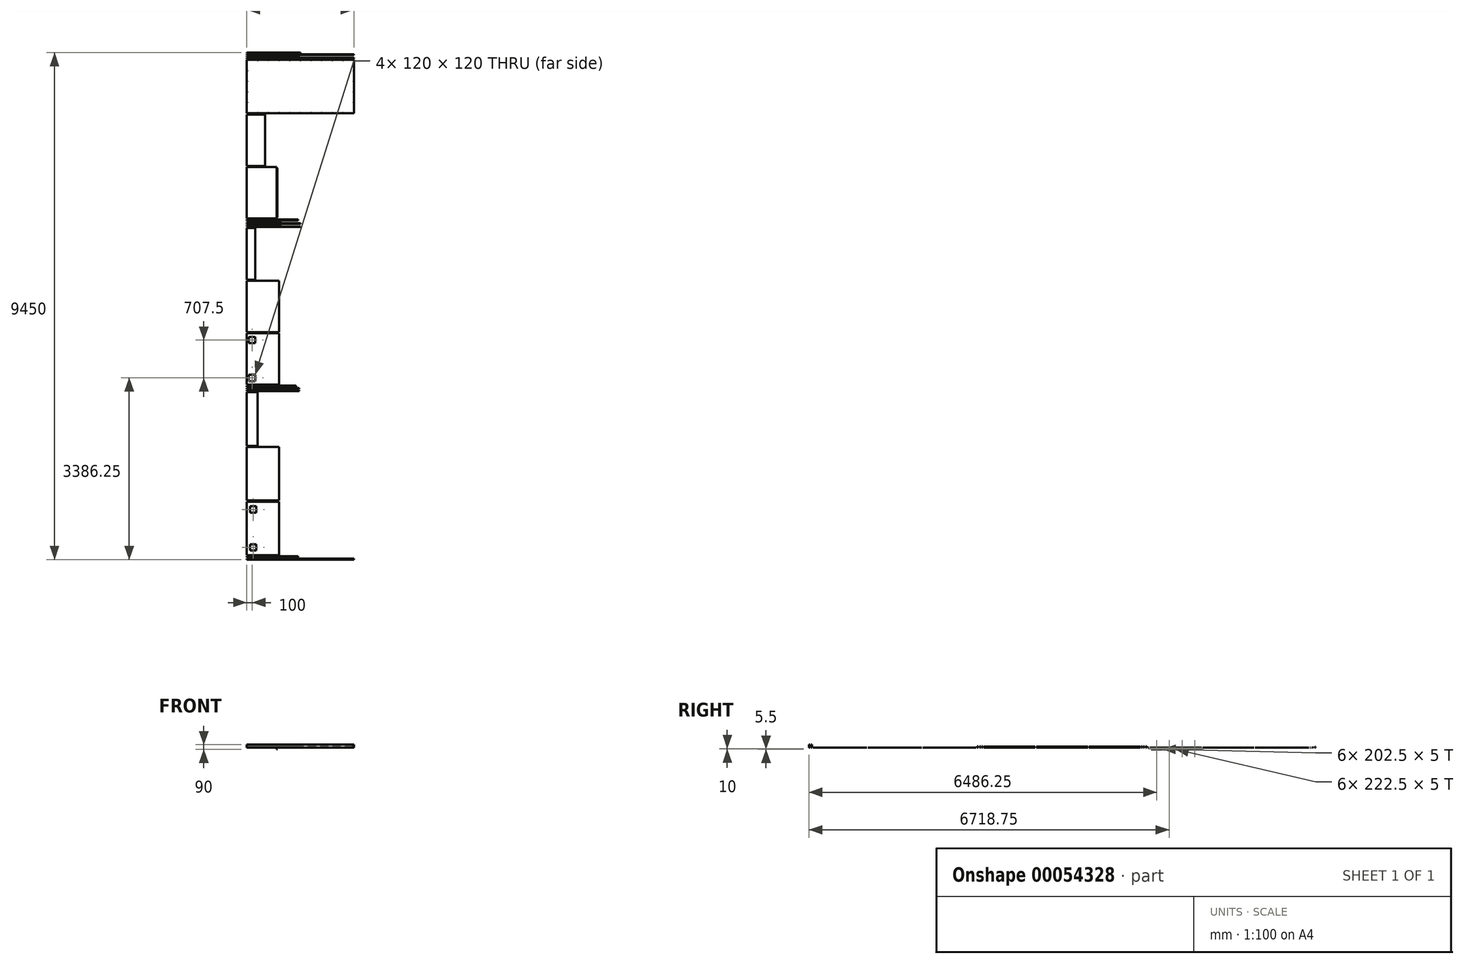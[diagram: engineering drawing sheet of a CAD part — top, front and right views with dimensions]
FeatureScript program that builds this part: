
annotation { "Feature Type Name" : "Feature", "Feature Type Description" : "" }
export const myFeature = defineFeature(function(context is Context, id is Id, definition is map)
    precondition{}
    {
        {
            var Q0;
            Q0=qCreatedBy(makeId("Right.planeOp"),FACE);
            var sketch = newSketch(context, id + "F0", { "sketchPlane" : qUnion([Q0])});
            skLineSegment(sketch, "E0.bottom", {"start": v(0, 60) * mm, "end": v(20, 60) * mm});
            skLineSegment(sketch, "E0.top", {"start": v(0, 0) * mm, "end": v(20, 0) * mm});
            skLineSegment(sketch, "E0.left", {"start": v(0, 60) * mm, "end": v(0, 0) * mm});
            skLineSegment(sketch, "E0.right", {"start": v(20, 60) * mm, "end": v(20, 0) * mm});
            skLineSegment(sketch, "E1.bottom", {"start": v(40, 0) * mm, "end": v(60, 0) * mm});
            skLineSegment(sketch, "E1.top", {"start": v(40, 60) * mm, "end": v(60, 60) * mm});
            skLineSegment(sketch, "E1.left", {"start": v(40, 0) * mm, "end": v(40, 60) * mm});
            skLineSegment(sketch, "E1.right", {"start": v(60, 0) * mm, "end": v(60, 60) * mm});
            skLineSegment(sketch, "E2.bottom", {"start": v(80, 0) * mm, "end": v(1080, 0) * mm});
            skLineSegment(sketch, "E2.top", {"start": v(80, 3) * mm, "end": v(1080, 3) * mm});
            skLineSegment(sketch, "E2.left", {"start": v(80, 0) * mm, "end": v(80, 3) * mm});
            skLineSegment(sketch, "E2.right", {"start": v(1080, 0) * mm, "end": v(1080, 3) * mm});
            skLineSegment(sketch, "E3.bottom", {"start": v(1100, 0) * mm, "end": v(2100, 0) * mm});
            skLineSegment(sketch, "E3.top", {"start": v(1100, 3) * mm, "end": v(2100, 3) * mm});
            skLineSegment(sketch, "E3.left", {"start": v(1100, 0) * mm, "end": v(1100, 3) * mm});
            skLineSegment(sketch, "E3.right", {"start": v(2100, 0) * mm, "end": v(2100, 3) * mm});
            skLineSegment(sketch, "E4.bottom", {"start": v(2120, 0) * mm, "end": v(3120, 0) * mm});
            skLineSegment(sketch, "E4.top", {"start": v(2120, 3) * mm, "end": v(3120, 3) * mm});
            skLineSegment(sketch, "E4.left", {"start": v(2120, 0) * mm, "end": v(2120, 3) * mm});
            skLineSegment(sketch, "E4.right", {"start": v(3120, 0) * mm, "end": v(3120, 3) * mm});
            skLineSegment(sketch, "E5.bottom", {"start": v(3140, 0) * mm, "end": v(3160, 0) * mm});
            skLineSegment(sketch, "E5.top", {"start": v(3140, 30) * mm, "end": v(3160, 30) * mm});
            skLineSegment(sketch, "E5.left", {"start": v(3140, 0) * mm, "end": v(3140, 30) * mm});
            skLineSegment(sketch, "E5.right", {"start": v(3160, 0) * mm, "end": v(3160, 30) * mm});
            skLineSegment(sketch, "E6.bottom", {"start": v(3220, 0) * mm, "end": v(3240, 0) * mm});
            skLineSegment(sketch, "E6.top", {"start": v(3220, 30) * mm, "end": v(3240, 30) * mm});
            skLineSegment(sketch, "E6.left", {"start": v(3220, 0) * mm, "end": v(3220, 30) * mm});
            skLineSegment(sketch, "E6.right", {"start": v(3240, 0) * mm, "end": v(3240, 30) * mm});
            skLineSegment(sketch, "E7.bottom", {"start": v(3260, 0) * mm, "end": v(4220, 0) * mm});
            skLineSegment(sketch, "E7.top", {"start": v(3260, 20) * mm, "end": v(4220, 20) * mm});
            skLineSegment(sketch, "E7.left", {"start": v(3260, 0) * mm, "end": v(3260, 20) * mm});
            skLineSegment(sketch, "E7.right", {"start": v(4220, 0) * mm, "end": v(4220, 20) * mm});
            skLineSegment(sketch, "E8.bottom", {"start": v(4240, 0) * mm, "end": v(5200, 0) * mm});
            skLineSegment(sketch, "E8.top", {"start": v(4240, 20) * mm, "end": v(5200, 20) * mm});
            skLineSegment(sketch, "E8.left", {"start": v(4240, 0) * mm, "end": v(4240, 20) * mm});
            skLineSegment(sketch, "E8.right", {"start": v(5200, 0) * mm, "end": v(5200, 20) * mm});
            skLineSegment(sketch, "E9.bottom", {"start": v(5220, 0) * mm, "end": v(6180, 0) * mm});
            skLineSegment(sketch, "E9.top", {"start": v(5220, 20) * mm, "end": v(6180, 20) * mm});
            skLineSegment(sketch, "E9.left", {"start": v(5220, 0) * mm, "end": v(5220, 20) * mm});
            skLineSegment(sketch, "E9.right", {"start": v(6180, 0) * mm, "end": v(6180, 20) * mm});
            skLineSegment(sketch, "E10.bottom", {"start": v(6200, 0) * mm, "end": v(6210, 0) * mm});
            skLineSegment(sketch, "E10.top", {"start": v(6200, 30) * mm, "end": v(6210, 30) * mm});
            skLineSegment(sketch, "E10.left", {"start": v(6200, 0) * mm, "end": v(6200, 30) * mm});
            skLineSegment(sketch, "E10.right", {"start": v(6210, 0) * mm, "end": v(6210, 30) * mm});
            skLineSegment(sketch, "E11.bottom", {"start": v(6230, 0) * mm, "end": v(6240, 0) * mm});
            skLineSegment(sketch, "E11.top", {"start": v(6230, 30) * mm, "end": v(6240, 30) * mm});
            skLineSegment(sketch, "E11.left", {"start": v(6230, 0) * mm, "end": v(6230, 30) * mm});
            skLineSegment(sketch, "E11.right", {"start": v(6240, 0) * mm, "end": v(6240, 30) * mm});
            skLineSegment(sketch, "E12.bottom", {"start": v(3180, 0) * mm, "end": v(3200, 0) * mm});
            skLineSegment(sketch, "E12.top", {"start": v(3180, 30) * mm, "end": v(3200, 30) * mm});
            skLineSegment(sketch, "E12.left", {"start": v(3180, 0) * mm, "end": v(3180, 30) * mm});
            skLineSegment(sketch, "E12.right", {"start": v(3200, 0) * mm, "end": v(3200, 30) * mm});
            skLineSegment(sketch, "E13.bottom", {"start": v(6260, 0) * mm, "end": v(6270, 0) * mm});
            skLineSegment(sketch, "E13.top", {"start": v(6260, 30) * mm, "end": v(6270, 30) * mm});
            skLineSegment(sketch, "E13.left", {"start": v(6260, 0) * mm, "end": v(6260, 30) * mm});
            skLineSegment(sketch, "E13.right", {"start": v(6270, 0) * mm, "end": v(6270, 30) * mm});
            skLineSegment(sketch, "E14.bottom", {"start": v(6290, 0) * mm, "end": v(6300, 0) * mm});
            skLineSegment(sketch, "E14.top", {"start": v(6290, 30) * mm, "end": v(6300, 30) * mm});
            skLineSegment(sketch, "E14.left", {"start": v(6290, 0) * mm, "end": v(6290, 30) * mm});
            skLineSegment(sketch, "E14.right", {"start": v(6300, 0) * mm, "end": v(6300, 30) * mm});
            skLineSegment(sketch, "E15.bottom", {"start": v(6320, 0) * mm, "end": v(6340, 0) * mm});
            skLineSegment(sketch, "E15.top", {"start": v(6320, 3) * mm, "end": v(6340, 3) * mm});
            skLineSegment(sketch, "E15.left", {"start": v(6320, 0) * mm, "end": v(6320, 3) * mm});
            skLineSegment(sketch, "E15.right", {"start": v(6340, 0) * mm, "end": v(6340, 3) * mm});
            skLineSegment(sketch, "E16.bottom", {"start": v(6360, 0) * mm, "end": v(7320, 0) * mm});
            skLineSegment(sketch, "E16.top", {"start": v(6360, 1) * mm, "end": v(7320, 1) * mm});
            skLineSegment(sketch, "E16.left", {"start": v(6360, 0) * mm, "end": v(6360, 1) * mm});
            skLineSegment(sketch, "E16.right", {"start": v(7320, 0) * mm, "end": v(7320, 1) * mm});
            skLineSegment(sketch, "E17.bottom", {"start": v(7340, 0) * mm, "end": v(8300, 0) * mm});
            skLineSegment(sketch, "E17.top", {"start": v(7340, 1) * mm, "end": v(8300, 1) * mm});
            skLineSegment(sketch, "E17.left", {"start": v(7340, 0) * mm, "end": v(7340, 1) * mm});
            skLineSegment(sketch, "E17.right", {"start": v(8300, 0) * mm, "end": v(8300, 1) * mm});
            skLineSegment(sketch, "E18.bottom", {"start": v(8320, 0) * mm, "end": v(9320, 0) * mm});
            skLineSegment(sketch, "E18.top", {"start": v(8320, 5) * mm, "end": v(9320, 5) * mm});
            skLineSegment(sketch, "E18.left", {"start": v(8320, 0) * mm, "end": v(8320, 5) * mm});
            skLineSegment(sketch, "E18.right", {"start": v(9320, 0) * mm, "end": v(9320, 5) * mm});
            skLineSegment(sketch, "E19.bottom", {"start": v(9340, 0) * mm, "end": v(9355, 0) * mm});
            skLineSegment(sketch, "E19.top", {"start": v(9340, 3) * mm, "end": v(9355, 3) * mm});
            skLineSegment(sketch, "E19.left", {"start": v(9340, 0) * mm, "end": v(9340, 3) * mm});
            skLineSegment(sketch, "E19.right", {"start": v(9355, 0) * mm, "end": v(9355, 3) * mm});
            skLineSegment(sketch, "E20.bottom", {"start": v(9375, 0) * mm, "end": v(9390, 0) * mm});
            skLineSegment(sketch, "E20.top", {"start": v(9375, 3) * mm, "end": v(9390, 3) * mm});
            skLineSegment(sketch, "E20.left", {"start": v(9375, 0) * mm, "end": v(9375, 3) * mm});
            skLineSegment(sketch, "E20.right", {"start": v(9390, 0) * mm, "end": v(9390, 3) * mm});
            skLineSegment(sketch, "E21", {"start": v(9410, 0) * mm, "end": v(9410, 20) * mm});
            skLineSegment(sketch, "E22", {"start": v(9410, 20) * mm, "end": v(9412, 20) * mm});
            skLineSegment(sketch, "E23", {"start": v(9412, 20) * mm, "end": v(9412, 2) * mm});
            skLineSegment(sketch, "E24", {"start": v(9412, 2) * mm, "end": v(9420, 2) * mm});
            skLineSegment(sketch, "E25", {"start": v(9420, 2) * mm, "end": v(9420, 0) * mm});
            skLineSegment(sketch, "E26", {"start": v(9420, 0) * mm, "end": v(9410, 0) * mm});
            skLineSegment(sketch, "E27", {"start": v(9440, 0) * mm, "end": v(9440, 20) * mm});
            skLineSegment(sketch, "E28", {"start": v(9440, 20) * mm, "end": v(9442, 20) * mm});
            skLineSegment(sketch, "E29", {"start": v(9442, 20) * mm, "end": v(9442, 2) * mm});
            skLineSegment(sketch, "E30", {"start": v(9442, 2) * mm, "end": v(9450, 2) * mm});
            skLineSegment(sketch, "E31", {"start": v(9450, 2) * mm, "end": v(9450, 0) * mm});
            skLineSegment(sketch, "E32", {"start": v(9450, 0) * mm, "end": v(9440, 0) * mm});
            skSolve(sketch);
        }
        {
            var Q0;
            Q0=makeQuery(id+"F0.imprint","IMPRINT",FACE,{"disambiguationData":[TD([[makeQuery(id+"F0.imprint","IMPRINT",EDGE,{"derivedFrom":sQuery(id+"F0.wireOp",EDGE,"E0.bottom")}),-1.0]])]});
            extrude(context, id + "F1", {"entities" : qUnion([Q0]), "depth" : 2000 * mm});
        }
        {
            var Q0;
            Q0=makeQuery(id+"F1.opExtrude","SWEPT_FACE",FACE,{"disambiguationData":[OSD([sQuery(id+"F0.wireOp",EDGE,"E0.left")])]});
            var sketch = newSketch(context, id + "F2", { "sketchPlane" : qUnion([Q0])});
            skPoint(sketch, "E33", {"position": v(10, 20) * mm});
            skPoint(sketch, "E34.0.1.0", {"position": v(10, 40) * mm});
            skLineSegment(sketch, "E34.direction1", {"start": v(10, 20) * mm, "end": v(1980, 20) * mm, "construction": true});
            skLineSegment(sketch, "E34.direction2", {"start": v(10, 20) * mm, "end": v(10, 40) * mm, "construction": true});
            skPoint(sketch, "E35.0.1.0", {"position": v(1980, 20) * mm});
            skPoint(sketch, "E35.0.1.1", {"position": v(1980, 40) * mm});
            skSolve(sketch);
        }
        {
            var Q0;
            Q0=sQuery(id+"F2.wireOp",VERTEX,"E33");
            var Q1;
            Q1=sQuery(id+"F2.wireOp",VERTEX,"E34.0.1.0");
            var Q2;
            Q2=sQuery(id+"F2.wireOp",VERTEX,"E35.0.1.1");
            var Q3;
            Q3=sQuery(id+"F2.wireOp",VERTEX,"E35.0.1.0");
            var Q4;
            Q4=makeQuery(id+"F1.opExtrude","SWEPT_BODY",BODY,{"disambiguationData":[OSD([sQuery(id+"F0.wireOp",EDGE,"E0.bottom"),sQuery(id+"F0.wireOp",EDGE,"E0.top"),sQuery(id+"F0.wireOp",EDGE,"E0.left"),sQuery(id+"F0.wireOp",EDGE,"E0.right")])]});
            hole(context, id + "F3", {"style" : HoleStyle.SIMPLE, "endStyle" : HoleEndStyle.THROUGH, "holeDiameter" : 2 * mm, "tappedDepth" : 10.5 * mm, "tapClearance" : 3, "locations" : qUnion([Q0, Q1, Q2, Q3]), "scope" : qUnion([Q4])});
        }
        {
            var Q0;
            Q0=makeQuery(id+"F0.imprint","IMPRINT",FACE,{"disambiguationData":[TD([[makeQuery(id+"F0.imprint","IMPRINT",EDGE,{"derivedFrom":sQuery(id+"F0.wireOp",EDGE,"E1.bottom")}),1.0]])]});
            extrude(context, id + "F4", {"entities" : qUnion([Q0]), "depth" : (1000 - 40) * mm});
        }
        {
            var Q0;
            Q0=makeQuery(id+"F0.imprint","IMPRINT",FACE,{"disambiguationData":[TD([[makeQuery(id+"F0.imprint","IMPRINT",EDGE,{"derivedFrom":sQuery(id+"F0.wireOp",EDGE,"E1.bottom")}),1.0]])]});
            var sketch = newSketch(context, id + "F5", { "sketchPlane" : qUnion([Q0])});
            skPoint(sketch, "E36", {"position": v(50, 40) * mm});
            skPoint(sketch, "E37", {"position": v(50, 20) * mm});
            skSolve(sketch);
        }
        {
            var Q0;
            Q0=makeQuery(id+"F4.opExtrude","CAP_FACE",FACE,{"disambiguationData":[OSD([sQuery(id+"F0.wireOp",EDGE,"E1.bottom"),sQuery(id+"F0.wireOp",EDGE,"E1.top"),sQuery(id+"F0.wireOp",EDGE,"E1.left"),sQuery(id+"F0.wireOp",EDGE,"E1.right")])],"isStart":false});
            var sketch = newSketch(context, id + "F6", { "sketchPlane" : qUnion([Q0])});
            skPoint(sketch, "E38", {"position": v(50, 20) * mm});
            skPoint(sketch, "E39", {"position": v(50, 40) * mm});
            skSolve(sketch);
        }
        {
            var Q0;
            Q0=sQuery(id+"F5.wireOp",VERTEX,"E36");
            var Q1;
            Q1=sQuery(id+"F6.wireOp",VERTEX,"E39");
            var Q2;
            Q2=makeQuery(id+"F4.opExtrude","SWEPT_BODY",BODY,{"disambiguationData":[OSD([sQuery(id+"F0.wireOp",EDGE,"E1.bottom"),sQuery(id+"F0.wireOp",EDGE,"E1.top"),sQuery(id+"F0.wireOp",EDGE,"E1.left"),sQuery(id+"F0.wireOp",EDGE,"E1.right")])]});
            hole(context, id + "F7", {"style" : HoleStyle.SIMPLE, "endStyle" : HoleEndStyle.BLIND, "holeDiameter" : 2 * mm, "holeDepth" : 50 * mm, "tappedDepth" : 10.5 * mm, "tapClearance" : 3, "locations" : qUnion([Q0, Q1]), "scope" : qUnion([Q2])});
        }
        {
            var Q0;
            Q0=sQuery(id+"F5.wireOp",VERTEX,"E36");
            var Q1;
            Q1=sQuery(id+"F5.wireOp",VERTEX,"E37");
            var Q2;
            Q2=makeQuery(id+"F4.opExtrude","SWEPT_BODY",BODY,{"disambiguationData":[OSD([sQuery(id+"F0.wireOp",EDGE,"E1.bottom"),sQuery(id+"F0.wireOp",EDGE,"E1.top"),sQuery(id+"F0.wireOp",EDGE,"E1.left"),sQuery(id+"F0.wireOp",EDGE,"E1.right")])]});
            hole(context, id + "F8", {"style" : HoleStyle.SIMPLE, "endStyle" : HoleEndStyle.BLIND, "oppositeDirection" : true, "holeDiameter" : 2 * mm, "holeDepth" : 50 * mm, "tappedDepth" : 10.5 * mm, "tapClearance" : 3, "locations" : qUnion([Q0, Q1]), "scope" : qUnion([Q2])});
        }
        {
            var Q0;
            Q0=makeQuery(id+"F0.imprint","IMPRINT",FACE,{"disambiguationData":[TD([[makeQuery(id+"F0.imprint","IMPRINT",EDGE,{"derivedFrom":sQuery(id+"F0.wireOp",EDGE,"E2.bottom")}),1.0]])]});
            extrude(context, id + "F9", {"entities" : qUnion([Q0]), "depth" : 600 * mm});
        }
        {
            var Q0;
            Q0=makeQuery(id+"F9.opExtrude","SWEPT_FACE",FACE,{"disambiguationData":[OSD([sQuery(id+"F0.wireOp",EDGE,"E2.top")])]});
            var sketch = newSketch(context, id + "F10", { "sketchPlane" : qUnion([Q0])});
            skLineSegment(sketch, "E40.bottom", {"start": v(60, 166.25) * mm, "end": v(180, 166.25) * mm});
            skLineSegment(sketch, "E40.top", {"start": v(60, 286.25) * mm, "end": v(180, 286.25) * mm});
            skLineSegment(sketch, "E40.left", {"start": v(60, 166.25) * mm, "end": v(60, 286.25) * mm});
            skLineSegment(sketch, "E40.right", {"start": v(180, 166.25) * mm, "end": v(180, 286.25) * mm});
            skLineSegment(sketch, "E41.bottom", {"start": v(60, 873.75) * mm, "end": v(180, 873.75) * mm});
            skLineSegment(sketch, "E41.top", {"start": v(60, 993.75) * mm, "end": v(180, 993.75) * mm});
            skLineSegment(sketch, "E41.left", {"start": v(60, 873.75) * mm, "end": v(60, 993.75) * mm});
            skLineSegment(sketch, "E41.right", {"start": v(180, 873.75) * mm, "end": v(180, 993.75) * mm});
            skSolve(sketch);
        }
        {
            var Q0;
            Q0=makeQuery(id+"F10.imprint","IMPRINT",FACE,{"disambiguationData":[TD([[makeQuery(id+"F10.imprint","IMPRINT",EDGE,{"derivedFrom":sQuery(id+"F10.wireOp",EDGE,"E40.bottom")}),1.0]])]});
            var Q1;
            Q1=makeQuery(id+"F10.imprint","IMPRINT",FACE,{"disambiguationData":[TD([[makeQuery(id+"F10.imprint","IMPRINT",EDGE,{"derivedFrom":sQuery(id+"F10.wireOp",EDGE,"E41.bottom")}),1.0]])]});
            extrude(context, id + "F11", {"entities" : qUnion([Q0, Q1]), "operationType" : NewBodyOperationType.REMOVE, "endBound" : BoundingType.UP_TO_NEXT, "oppositeDirection" : true, "depth" : 25 * mm});
        }
        {
            var Q0;
            Q0=makeQuery(id+"F0.imprint","IMPRINT",FACE,{"disambiguationData":[TD([[makeQuery(id+"F0.imprint","IMPRINT",EDGE,{"derivedFrom":sQuery(id+"F0.wireOp",EDGE,"E3.bottom")}),1.0]])]});
            var Q1;
            Q1=makeQuery(id+"F9.opExtrude","CAP_FACE",FACE,{"disambiguationData":[OSD([sQuery(id+"F0.wireOp",EDGE,"E2.bottom"),sQuery(id+"F0.wireOp",EDGE,"E2.top"),sQuery(id+"F0.wireOp",EDGE,"E2.left"),sQuery(id+"F0.wireOp",EDGE,"E2.right")])],"isStart":false});
            extrude(context, id + "F12", {"entities" : qUnion([Q0]), "endBound" : BoundingType.UP_TO_SURFACE, "endBoundEntityFace" : qUnion([Q1]), "depth" : 25 * mm});
        }
        {
            var Q0;
            Q0=makeQuery(id+"F0.imprint","IMPRINT",FACE,{"disambiguationData":[TD([[makeQuery(id+"F0.imprint","IMPRINT",EDGE,{"derivedFrom":sQuery(id+"F0.wireOp",EDGE,"E4.bottom")}),1.0]])]});
            extrude(context, id + "F13", {"entities" : qUnion([Q0]), "depth" : 200 * mm});
        }
        {
            var Q0;
            Q0=makeQuery(id+"F0.imprint","IMPRINT",FACE,{"disambiguationData":[TD([[makeQuery(id+"F0.imprint","IMPRINT",EDGE,{"derivedFrom":sQuery(id+"F0.wireOp",EDGE,"E5.bottom")}),1.0]])]});
            extrude(context, id + "F14", {"entities" : qUnion([Q0]), "depth" : (1000 - 20) * mm});
        }
        {
            var Q0;
            Q0=makeQuery(id+"F0.imprint","IMPRINT",FACE,{"disambiguationData":[TD([[makeQuery(id+"F0.imprint","IMPRINT",EDGE,{"derivedFrom":sQuery(id+"F0.wireOp",EDGE,"E6.bottom")}),1.0]])]});
            extrude(context, id + "F15", {"entities" : qUnion([Q0]), "depth" : (960 - 40) * mm});
        }
        {
            var Q0;
            Q0=makeQuery(id+"F0.imprint","IMPRINT",FACE,{"disambiguationData":[TD([[makeQuery(id+"F0.imprint","IMPRINT",EDGE,{"derivedFrom":sQuery(id+"F0.wireOp",EDGE,"E7.bottom")}),1.0]])]});
            extrude(context, id + "F16", {"entities" : qUnion([Q0]), "depth" : 600 * mm});
        }
        {
            var Q0;
            Q0=makeQuery(id+"F16.opExtrude","SWEPT_FACE",FACE,{"disambiguationData":[OSD([sQuery(id+"F0.wireOp",EDGE,"E7.top")])]});
            var sketch = newSketch(context, id + "F17", { "sketchPlane" : qUnion([Q0])});
            skLineSegment(sketch, "E42.bottom", {"start": v(40, 3326.25) * mm, "end": v(160, 3326.25) * mm});
            skLineSegment(sketch, "E42.top", {"start": v(40, 3446.25) * mm, "end": v(160, 3446.25) * mm});
            skLineSegment(sketch, "E42.left", {"start": v(40, 3326.25) * mm, "end": v(40, 3446.25) * mm});
            skLineSegment(sketch, "E42.right", {"start": v(160, 3326.25) * mm, "end": v(160, 3446.25) * mm});
            skLineSegment(sketch, "E43.bottom", {"start": v(160, 4033.75) * mm, "end": v(40, 4033.75) * mm});
            skLineSegment(sketch, "E43.top", {"start": v(160, 4153.75) * mm, "end": v(40, 4153.75) * mm});
            skLineSegment(sketch, "E43.left", {"start": v(160, 4033.75) * mm, "end": v(160, 4153.75) * mm});
            skLineSegment(sketch, "E43.right", {"start": v(40, 4033.75) * mm, "end": v(40, 4153.75) * mm});
            skSolve(sketch);
        }
        {
            var Q0;
            Q0=makeQuery(id+"F17.imprint","IMPRINT",FACE,{"disambiguationData":[TD([[makeQuery(id+"F17.imprint","IMPRINT",EDGE,{"derivedFrom":sQuery(id+"F17.wireOp",EDGE,"E42.bottom")}),1.0]])]});
            var Q1;
            Q1=makeQuery(id+"F17.imprint","IMPRINT",FACE,{"disambiguationData":[TD([[makeQuery(id+"F17.imprint","IMPRINT",EDGE,{"derivedFrom":sQuery(id+"F17.wireOp",EDGE,"E43.bottom")}),-1.0]])]});
            extrude(context, id + "F18", {"entities" : qUnion([Q0, Q1]), "operationType" : NewBodyOperationType.REMOVE, "endBound" : BoundingType.UP_TO_NEXT, "oppositeDirection" : true, "depth" : 25 * mm});
        }
        {
            var Q0;
            Q0=makeQuery(id+"F0.imprint","IMPRINT",FACE,{"disambiguationData":[TD([[makeQuery(id+"F0.imprint","IMPRINT",EDGE,{"derivedFrom":sQuery(id+"F0.wireOp",EDGE,"E8.bottom")}),1.0]])]});
            extrude(context, id + "F19", {"entities" : qUnion([Q0]), "depth" : 600 * mm});
        }
        {
            var Q0;
            Q0=makeQuery(id+"F0.imprint","IMPRINT",FACE,{"disambiguationData":[TD([[makeQuery(id+"F0.imprint","IMPRINT",EDGE,{"derivedFrom":sQuery(id+"F0.wireOp",EDGE,"E9.bottom")}),1.0]])]});
            extrude(context, id + "F20", {"entities" : qUnion([Q0]), "depth" : (200 - 40) * mm});
        }
        {
            var Q0;
            Q0=makeQuery(id+"F0.imprint","IMPRINT",FACE,{"disambiguationData":[TD([[makeQuery(id+"F0.imprint","IMPRINT",EDGE,{"derivedFrom":sQuery(id+"F0.wireOp",EDGE,"E10.bottom")}),1.0]])]});
            extrude(context, id + "F21", {"entities" : qUnion([Q0]), "depth" : 1000 * mm});
        }
        {
            var Q0;
            Q0=makeQuery(id+"F0.imprint","IMPRINT",FACE,{"disambiguationData":[TD([[makeQuery(id+"F0.imprint","IMPRINT",EDGE,{"derivedFrom":sQuery(id+"F0.wireOp",EDGE,"E11.bottom")}),1.0]])]});
            extrude(context, id + "F22", {"entities" : qUnion([Q0]), "depth" : 625 * mm});
        }
        {
            var Q0;
            Q0=makeQuery(id+"F14.opExtrude","SWEPT_FACE",FACE,{"disambiguationData":[OSD([sQuery(id+"F0.wireOp",EDGE,"E5.top")])]});
            var sketch = newSketch(context, id + "F23", { "sketchPlane" : qUnion([Q0])});
            skLineSegment(sketch, "E44.bottom", {"start": v(539, 3140) * mm, "end": v(559, 3140) * mm});
            skLineSegment(sketch, "E44.top", {"start": v(539, 3160) * mm, "end": v(559, 3160) * mm});
            skLineSegment(sketch, "E44.left", {"start": v(539, 3140) * mm, "end": v(539, 3160) * mm});
            skLineSegment(sketch, "E44.right", {"start": v(559, 3140) * mm, "end": v(559, 3160) * mm});
            skSolve(sketch);
        }
        {
            var Q0;
            Q0=makeQuery(id+"F23.imprint","IMPRINT",FACE,{"disambiguationData":[TD([[makeQuery(id+"F23.imprint","IMPRINT",EDGE,{"derivedFrom":sQuery(id+"F23.wireOp",EDGE,"E44.bottom")}),-1.0]])]});
            extrude(context, id + "F24", {"entities" : qUnion([Q0]), "operationType" : NewBodyOperationType.REMOVE, "oppositeDirection" : true, "depth" : 3 * mm});
        }
        {
            var Q0;
            Q0=makeQuery(id+"F0.imprint","IMPRINT",FACE,{"disambiguationData":[TD([[makeQuery(id+"F0.imprint","IMPRINT",EDGE,{"derivedFrom":sQuery(id+"F0.wireOp",EDGE,"E12.bottom")}),1.0]])]});
            extrude(context, id + "F25", {"entities" : qUnion([Q0]), "depth" : 980 * mm});
        }
        {
            var Q0;
            Q0=makeQuery(id+"F25.opExtrude","SWEPT_FACE",FACE,{"disambiguationData":[OSD([sQuery(id+"F0.wireOp",EDGE,"E12.top")])]});
            var sketch = newSketch(context, id + "F26", { "sketchPlane" : qUnion([Q0])});
            skLineSegment(sketch, "E45.bottom", {"start": v(98, 3180) * mm, "end": v(118, 3180) * mm});
            skLineSegment(sketch, "E45.top", {"start": v(98, 3200) * mm, "end": v(118, 3200) * mm});
            skLineSegment(sketch, "E45.left", {"start": v(98, 3180) * mm, "end": v(98, 3200) * mm});
            skLineSegment(sketch, "E45.right", {"start": v(118, 3180) * mm, "end": v(118, 3200) * mm});
            skLineSegment(sketch, "E46.bottom", {"start": v(637, 3180) * mm, "end": v(657, 3180) * mm});
            skLineSegment(sketch, "E46.top", {"start": v(637, 3200) * mm, "end": v(657, 3200) * mm});
            skLineSegment(sketch, "E46.left", {"start": v(637, 3180) * mm, "end": v(637, 3200) * mm});
            skLineSegment(sketch, "E46.right", {"start": v(657, 3180) * mm, "end": v(657, 3200) * mm});
            skSolve(sketch);
        }
        {
            var Q0;
            Q0=makeQuery(id+"F26.imprint","IMPRINT",FACE,{"disambiguationData":[TD([[makeQuery(id+"F26.imprint","IMPRINT",EDGE,{"derivedFrom":sQuery(id+"F26.wireOp",EDGE,"E46.bottom")}),-1.0]])]});
            var Q1;
            Q1=makeQuery(id+"F26.imprint","IMPRINT",FACE,{"disambiguationData":[TD([[makeQuery(id+"F26.imprint","IMPRINT",EDGE,{"derivedFrom":sQuery(id+"F26.wireOp",EDGE,"E45.bottom")}),-1.0]])]});
            extrude(context, id + "F27", {"entities" : qUnion([Q0, Q1]), "operationType" : NewBodyOperationType.REMOVE, "oppositeDirection" : true, "depth" : 3 * mm});
        }
        {
            var Q0;
            Q0=makeQuery(id+"F21.opExtrude","SWEPT_FACE",FACE,{"disambiguationData":[OSD([sQuery(id+"F0.wireOp",EDGE,"E10.top")])]});
            var sketch = newSketch(context, id + "F28", { "sketchPlane" : qUnion([Q0])});
            skLineSegment(sketch, "E47.bottom", {"start": v(519, 6200) * mm, "end": v(539, 6200) * mm});
            skLineSegment(sketch, "E47.top", {"start": v(519, 6210) * mm, "end": v(539, 6210) * mm});
            skLineSegment(sketch, "E47.left", {"start": v(519, 6200) * mm, "end": v(519, 6210) * mm});
            skLineSegment(sketch, "E47.right", {"start": v(539, 6200) * mm, "end": v(539, 6210) * mm});
            skSolve(sketch);
        }
        {
            var Q0;
            Q0=makeQuery(id+"F28.imprint","IMPRINT",FACE,{"disambiguationData":[TD([[makeQuery(id+"F28.imprint","IMPRINT",EDGE,{"derivedFrom":sQuery(id+"F28.wireOp",EDGE,"E47.bottom")}),-1.0]])]});
            extrude(context, id + "F29", {"entities" : qUnion([Q0]), "operationType" : NewBodyOperationType.REMOVE, "oppositeDirection" : true, "depth" : 3 * mm});
        }
        {
            var Q0;
            Q0=makeQuery(id+"F22.opExtrude","SWEPT_FACE",FACE,{"disambiguationData":[OSD([sQuery(id+"F0.wireOp",EDGE,"E11.top")])]});
            var sketch = newSketch(context, id + "F30", { "sketchPlane" : qUnion([Q0])});
            skLineSegment(sketch, "E48.bottom", {"start": v(58, 6230) * mm, "end": v(78, 6230) * mm});
            skLineSegment(sketch, "E48.top", {"start": v(58, 6240) * mm, "end": v(78, 6240) * mm});
            skLineSegment(sketch, "E48.left", {"start": v(58, 6230) * mm, "end": v(58, 6240) * mm});
            skLineSegment(sketch, "E48.right", {"start": v(78, 6230) * mm, "end": v(78, 6240) * mm});
            skLineSegment(sketch, "E49.bottom", {"start": v(597, 6230) * mm, "end": v(617, 6230) * mm});
            skLineSegment(sketch, "E49.top", {"start": v(597, 6240) * mm, "end": v(617, 6240) * mm});
            skLineSegment(sketch, "E49.left", {"start": v(597, 6230) * mm, "end": v(597, 6240) * mm});
            skLineSegment(sketch, "E49.right", {"start": v(617, 6230) * mm, "end": v(617, 6240) * mm});
            skSolve(sketch);
        }
        {
            var Q0;
            Q0=makeQuery(id+"F30.imprint","IMPRINT",FACE,{"disambiguationData":[TD([[makeQuery(id+"F30.imprint","IMPRINT",EDGE,{"derivedFrom":sQuery(id+"F30.wireOp",EDGE,"E48.bottom")}),-1.0]])]});
            var Q1;
            Q1=makeQuery(id+"F30.imprint","IMPRINT",FACE,{"disambiguationData":[TD([[makeQuery(id+"F30.imprint","IMPRINT",EDGE,{"derivedFrom":sQuery(id+"F30.wireOp",EDGE,"E49.bottom")}),-1.0]])]});
            extrude(context, id + "F31", {"entities" : qUnion([Q0, Q1]), "operationType" : NewBodyOperationType.REMOVE, "oppositeDirection" : true, "depth" : 3 * mm});
        }
        {
            var Q0;
            Q0=makeQuery(id+"F0.imprint","IMPRINT",FACE,{"disambiguationData":[TD([[makeQuery(id+"F0.imprint","IMPRINT",EDGE,{"derivedFrom":sQuery(id+"F0.wireOp",EDGE,"E13.bottom")}),1.0]])]});
            var Q1;
            Q1=makeQuery(id+"F21.opExtrude","CAP_FACE",FACE,{"disambiguationData":[OSD([sQuery(id+"F0.wireOp",EDGE,"E10.bottom"),sQuery(id+"F0.wireOp",EDGE,"E10.top"),sQuery(id+"F0.wireOp",EDGE,"E10.left"),sQuery(id+"F0.wireOp",EDGE,"E10.right")])],"isStart":false});
            extrude(context, id + "F32", {"entities" : qUnion([Q0]), "endBound" : BoundingType.UP_TO_SURFACE, "endBoundEntityFace" : qUnion([Q1]), "depth" : 1000 * mm});
        }
        {
            var Q0;
            Q0=makeQuery(id+"F0.imprint","IMPRINT",FACE,{"disambiguationData":[TD([[makeQuery(id+"F0.imprint","IMPRINT",EDGE,{"derivedFrom":sQuery(id+"F0.wireOp",EDGE,"E14.bottom")}),1.0]])]});
            var Q1;
            Q1=makeQuery(id+"F22.opExtrude","CAP_FACE",FACE,{"disambiguationData":[OSD([sQuery(id+"F0.wireOp",EDGE,"E11.bottom"),sQuery(id+"F0.wireOp",EDGE,"E11.top"),sQuery(id+"F0.wireOp",EDGE,"E11.left"),sQuery(id+"F0.wireOp",EDGE,"E11.right")])],"isStart":false});
            extrude(context, id + "F33", {"entities" : qUnion([Q0]), "endBound" : BoundingType.UP_TO_SURFACE, "endBoundEntityFace" : qUnion([Q1]), "depth" : 25 * mm});
        }
        {
            var Q0;
            Q0=makeQuery(id+"F32.opExtrude","SWEPT_FACE",FACE,{"disambiguationData":[OSD([sQuery(id+"F0.wireOp",EDGE,"E13.top")])]});
            var sketch = newSketch(context, id + "F34", { "sketchPlane" : qUnion([Q0])});
            skLineSegment(sketch, "E50.bottom", {"start": v(303, 6260) * mm, "end": v(323, 6260) * mm});
            skLineSegment(sketch, "E50.top", {"start": v(303, 6270) * mm, "end": v(323, 6270) * mm});
            skLineSegment(sketch, "E50.left", {"start": v(303, 6260) * mm, "end": v(303, 6270) * mm});
            skLineSegment(sketch, "E50.right", {"start": v(323, 6260) * mm, "end": v(323, 6270) * mm});
            skLineSegment(sketch, "E51.bottom", {"start": v(842, 6260) * mm, "end": v(862, 6260) * mm});
            skLineSegment(sketch, "E51.top", {"start": v(842, 6270) * mm, "end": v(862, 6270) * mm});
            skLineSegment(sketch, "E51.left", {"start": v(842, 6260) * mm, "end": v(842, 6270) * mm});
            skLineSegment(sketch, "E51.right", {"start": v(862, 6260) * mm, "end": v(862, 6270) * mm});
            skSolve(sketch);
        }
        {
            var Q0;
            Q0=makeQuery(id+"F34.imprint","IMPRINT",FACE,{"disambiguationData":[TD([[makeQuery(id+"F34.imprint","IMPRINT",EDGE,{"derivedFrom":sQuery(id+"F34.wireOp",EDGE,"E50.bottom")}),-1.0]])]});
            var Q1;
            Q1=makeQuery(id+"F34.imprint","IMPRINT",FACE,{"disambiguationData":[TD([[makeQuery(id+"F34.imprint","IMPRINT",EDGE,{"derivedFrom":sQuery(id+"F34.wireOp",EDGE,"E51.bottom")}),-1.0]])]});
            extrude(context, id + "F35", {"entities" : qUnion([Q0, Q1]), "operationType" : NewBodyOperationType.REMOVE, "oppositeDirection" : true, "depth" : 3 * mm});
        }
        {
            var Q0;
            Q0=makeQuery(id+"F33.opExtrude","SWEPT_FACE",FACE,{"disambiguationData":[OSD([sQuery(id+"F0.wireOp",EDGE,"E14.top")])]});
            var sketch = newSketch(context, id + "F36", { "sketchPlane" : qUnion([Q0])});
            skLineSegment(sketch, "E52.bottom", {"start": v(381, 6290) * mm, "end": v(401, 6290) * mm});
            skLineSegment(sketch, "E52.top", {"start": v(381, 6300) * mm, "end": v(401, 6300) * mm});
            skLineSegment(sketch, "E52.left", {"start": v(381, 6290) * mm, "end": v(381, 6300) * mm});
            skLineSegment(sketch, "E52.right", {"start": v(401, 6290) * mm, "end": v(401, 6300) * mm});
            skSolve(sketch);
        }
        {
            var Q0;
            Q0=makeQuery(id+"F36.imprint","IMPRINT",FACE,{"disambiguationData":[TD([[makeQuery(id+"F36.imprint","IMPRINT",EDGE,{"derivedFrom":sQuery(id+"F36.wireOp",EDGE,"E52.bottom")}),-1.0]])]});
            extrude(context, id + "F37", {"entities" : qUnion([Q0]), "operationType" : NewBodyOperationType.REMOVE, "oppositeDirection" : true, "depth" : 3 * mm});
        }
        {
            var Q0;
            Q0=makeQuery(id+"F0.imprint","IMPRINT",FACE,{"disambiguationData":[TD([[makeQuery(id+"F0.imprint","IMPRINT",EDGE,{"derivedFrom":sQuery(id+"F0.wireOp",EDGE,"E15.bottom")}),1.0]])]});
            extrude(context, id + "F38", {"entities" : qUnion([Q0]), "depth" : (1000 - 40) * mm});
        }
        {
            var Q0;
            Q0=makeQuery(id+"F0.imprint","IMPRINT",FACE,{"disambiguationData":[TD([[makeQuery(id+"F0.imprint","IMPRINT",EDGE,{"derivedFrom":sQuery(id+"F0.wireOp",EDGE,"E16.bottom")}),1.0]])]});
            extrude(context, id + "F39", {"entities" : qUnion([Q0]), "depth" : 560 * mm});
        }
        {
            var Q0;
            Q0=makeQuery(id+"F39.opExtrude","SWEPT_FACE",FACE,{"disambiguationData":[OSD([sQuery(id+"F0.wireOp",EDGE,"E16.right")])]});
            var sketch = newSketch(context, id + "F40", { "sketchPlane" : qUnion([Q0])});
            skLineSegment(sketch, "E53", {"start": v(-560, 0) * mm, "end": v(-560, -29) * mm});
            skLineSegment(sketch, "E54", {"start": v(-560, -29) * mm, "end": v(-570, -29) * mm});
            skLineSegment(sketch, "E55", {"start": v(-570, -29) * mm, "end": v(-570, -30) * mm});
            skLineSegment(sketch, "E56", {"start": v(-570, -30) * mm, "end": v(-559, -30) * mm});
            skLineSegment(sketch, "E57", {"start": v(-559, -30) * mm, "end": v(-559, 0) * mm});
            skSolve(sketch);
        }
        {
            var Q0;
            {var subQ0=sQuery(id+"F40.wireOp",EDGE,"E53");Q0=makeQuery(id+"F40.imprint","IMPRINT",FACE,{"disambiguationData":[TD([[makeQuery(id+"F40.imprint","IMPRINT",EDGE,{"derivedFrom":subQ0}),1.0]])]});}
            var Q1;
            Q1=makeQuery(id+"F39.opExtrude","SWEPT_FACE",FACE,{"disambiguationData":[OSD([sQuery(id+"F0.wireOp",EDGE,"E16.left")])]});
            extrude(context, id + "F41", {"entities" : qUnion([Q0]), "operationType" : NewBodyOperationType.ADD, "endBound" : BoundingType.UP_TO_SURFACE, "oppositeDirection" : true, "endBoundEntityFace" : qUnion([Q1]), "depth" : 25 * mm});
        }
        {
            var Q0;
            Q0=makeQuery(id+"F41.opExtrude","SWEPT_FACE",FACE,{"disambiguationData":[OSD([sQuery(id+"F40.wireOp",EDGE,"E55")])]});
            var sketch = newSketch(context, id + "F42", { "sketchPlane" : qUnion([Q0])});
            skLineSegment(sketch, "E58.bottom", {"start": v(6360, -30) * mm, "end": v(6380, -30) * mm});
            skLineSegment(sketch, "E58.top", {"start": v(6360, 1) * mm, "end": v(6380, 1) * mm});
            skLineSegment(sketch, "E58.left", {"start": v(6360, -30) * mm, "end": v(6360, 1) * mm});
            skLineSegment(sketch, "E58.right", {"start": v(6380, -30) * mm, "end": v(6380, 1) * mm});
            skLineSegment(sketch, "E59.bottom", {"start": v(7320, -30) * mm, "end": v(7300, -30) * mm});
            skLineSegment(sketch, "E59.top", {"start": v(7320, 1) * mm, "end": v(7300, 1) * mm});
            skLineSegment(sketch, "E59.left", {"start": v(7320, -30) * mm, "end": v(7320, 1) * mm});
            skLineSegment(sketch, "E59.right", {"start": v(7300, -30) * mm, "end": v(7300, 1) * mm});
            skLineSegment(sketch, "E60.bottom", {"start": v(6592.5, -30) * mm, "end": v(6602.5, -30) * mm});
            skLineSegment(sketch, "E60.top", {"start": v(6592.5, 1) * mm, "end": v(6602.5, 1) * mm});
            skLineSegment(sketch, "E60.left", {"start": v(6592.5, -30) * mm, "end": v(6592.5, 1) * mm});
            skLineSegment(sketch, "E60.right", {"start": v(6602.5, -30) * mm, "end": v(6602.5, 1) * mm});
            skLineSegment(sketch, "E61.bottom", {"start": v(6835, -30) * mm, "end": v(6845, -30) * mm});
            skLineSegment(sketch, "E61.top", {"start": v(6835, 1) * mm, "end": v(6845, 1) * mm});
            skLineSegment(sketch, "E61.left", {"start": v(6835, -30) * mm, "end": v(6835, 1) * mm});
            skLineSegment(sketch, "E61.right", {"start": v(6845, -30) * mm, "end": v(6845, 1) * mm});
            skLineSegment(sketch, "E62.bottom", {"start": v(7077.5, -30) * mm, "end": v(7087.5, -30) * mm});
            skLineSegment(sketch, "E62.top", {"start": v(7077.5, 1) * mm, "end": v(7087.5, 1) * mm});
            skLineSegment(sketch, "E62.left", {"start": v(7077.5, -30) * mm, "end": v(7077.5, 1) * mm});
            skLineSegment(sketch, "E62.right", {"start": v(7087.5, -30) * mm, "end": v(7087.5, 1) * mm});
            skSolve(sketch);
        }
        {
            var Q0;
            {var subQ0=sQuery(id+"F42.wireOp",EDGE,"E58.bottom");Q0=makeQuery(id+"F42.imprint","IMPRINT",FACE,{"disambiguationData":[TD([[makeQuery(id+"F42.imprint","IMPRINT",EDGE,{"derivedFrom":subQ0}),1.0]])]});}
            var Q1;
            {var subQ0=sQuery(id+"F42.wireOp",EDGE,"E58.top");Q1=makeQuery(id+"F42.imprint","IMPRINT",FACE,{"disambiguationData":[TD([[makeQuery(id+"F42.imprint","IMPRINT",EDGE,{"derivedFrom":subQ0}),-1.0]])]});}
            var Q2;
            {var subQ0=sQuery(id+"F42.wireOp",EDGE,"E59.top");Q2=makeQuery(id+"F42.imprint","IMPRINT",FACE,{"disambiguationData":[TD([[makeQuery(id+"F42.imprint","IMPRINT",EDGE,{"derivedFrom":subQ0}),1.0]])]});}
            var Q3;
            {var subQ0=sQuery(id+"F42.wireOp",EDGE,"E59.bottom");Q3=makeQuery(id+"F42.imprint","IMPRINT",FACE,{"disambiguationData":[TD([[makeQuery(id+"F42.imprint","IMPRINT",EDGE,{"derivedFrom":subQ0}),1.0]])]});}
            var Q4;
            {var subQ0=sQuery(id+"F42.wireOp",EDGE,"E60.top");Q4=makeQuery(id+"F42.imprint","IMPRINT",FACE,{"disambiguationData":[TD([[makeQuery(id+"F42.imprint","IMPRINT",EDGE,{"derivedFrom":subQ0}),-1.0]])]});}
            var Q5;
            {var subQ0=sQuery(id+"F42.wireOp",EDGE,"E61.top");Q5=makeQuery(id+"F42.imprint","IMPRINT",FACE,{"disambiguationData":[TD([[makeQuery(id+"F42.imprint","IMPRINT",EDGE,{"derivedFrom":subQ0}),-1.0]])]});}
            var Q6;
            {var subQ0=sQuery(id+"F42.wireOp",EDGE,"E62.top");Q6=makeQuery(id+"F42.imprint","IMPRINT",FACE,{"disambiguationData":[TD([[makeQuery(id+"F42.imprint","IMPRINT",EDGE,{"derivedFrom":subQ0}),-1.0]])]});}
            var Q7;
            {var subQ0=sQuery(id+"F42.wireOp",EDGE,"E60.bottom");Q7=makeQuery(id+"F42.imprint","IMPRINT",FACE,{"disambiguationData":[TD([[makeQuery(id+"F42.imprint","IMPRINT",EDGE,{"derivedFrom":subQ0}),1.0]])]});}
            var Q8;
            {var subQ0=sQuery(id+"F42.wireOp",EDGE,"E61.bottom");Q8=makeQuery(id+"F42.imprint","IMPRINT",FACE,{"disambiguationData":[TD([[makeQuery(id+"F42.imprint","IMPRINT",EDGE,{"derivedFrom":subQ0}),1.0]])]});}
            var Q9;
            {var subQ0=sQuery(id+"F42.wireOp",EDGE,"E62.bottom");Q9=makeQuery(id+"F42.imprint","IMPRINT",FACE,{"disambiguationData":[TD([[makeQuery(id+"F42.imprint","IMPRINT",EDGE,{"derivedFrom":subQ0}),1.0]])]});}
            var Q10;
            Q10=makeQuery(id+"F41.opExtrude","SWEPT_FACE",FACE,{"disambiguationData":[OSD([sQuery(id+"F40.wireOp",EDGE,"E57")])]});
            extrude(context, id + "F43", {"entities" : qUnion([Q0, Q1, Q2, Q3, Q4, Q5, Q6, Q7, Q8, Q9]), "operationType" : NewBodyOperationType.REMOVE, "endBound" : BoundingType.UP_TO_SURFACE, "oppositeDirection" : true, "endBoundEntityFace" : qUnion([Q10]), "depth" : 25 * mm});
        }
        {
            var Q0;
            {var subQ0=sQuery(id+"F0.wireOp",EDGE,"E16.top");Q0=makeQuery(id+"F43.boolean.opBoolean","SPLIT",FACE,{"disambiguationData":[TD([makeQuery(id+"F43.opExtrude","SWEPT_FACE",FACE,{"disambiguationData":[OSD([sQuery(id+"F42.wireOp",EDGE,"E58.right")])]})])],"derivedFrom":makeQuery(id+"F41.boolean.opBoolean","MERGE",FACE,{"derivedFrom":[makeQuery(id+"F39.opExtrude","CAP_FACE",FACE,{"disambiguationData":[OSD([sQuery(id+"F0.wireOp",EDGE,"E16.bottom"),subQ0,sQuery(id+"F0.wireOp",EDGE,"E16.left"),sQuery(id+"F0.wireOp",EDGE,"E16.right")])],"isStart":false}),makeQuery(id+"F41.opExtrude","SWEPT_FACE",FACE,{"disambiguationData":[OSD([sQuery(id+"F40.wireOp",EDGE,"E53")])]})]})});}
            var sketch = newSketch(context, id + "F44", { "sketchPlane" : qUnion([Q0])});
            skLineSegment(sketch, "E63.bottom", {"start": v(6385, -22) * mm, "end": v(6587.5, -22) * mm});
            skLineSegment(sketch, "E63.top", {"start": v(6385, -27) * mm, "end": v(6587.5, -27) * mm});
            skLineSegment(sketch, "E63.left", {"start": v(6385, -22) * mm, "end": v(6385, -27) * mm});
            skLineSegment(sketch, "E63.right", {"start": v(6587.5, -22) * mm, "end": v(6587.5, -27) * mm});
            skLineSegment(sketch, "E64.0.1.0", {"start": v(6385, -12) * mm, "end": v(6587.5, -12) * mm});
            skLineSegment(sketch, "E64.0.1.1", {"start": v(6385, -17) * mm, "end": v(6587.5, -17) * mm});
            skLineSegment(sketch, "E64.0.1.2", {"start": v(6385, -12) * mm, "end": v(6385, -17) * mm});
            skLineSegment(sketch, "E64.0.1.3", {"start": v(6587.5, -12) * mm, "end": v(6587.5, -17) * mm});
            skLineSegment(sketch, "E64.0.2.0", {"start": v(6385, -2) * mm, "end": v(6587.5, -2) * mm});
            skLineSegment(sketch, "E64.0.2.1", {"start": v(6385, -7) * mm, "end": v(6587.5, -7) * mm});
            skLineSegment(sketch, "E64.0.2.2", {"start": v(6385, -2) * mm, "end": v(6385, -7) * mm});
            skLineSegment(sketch, "E64.0.2.3", {"start": v(6587.5, -2) * mm, "end": v(6587.5, -7) * mm});
            skLineSegment(sketch, "E64.direction1", {"start": v(6385, -22) * mm, "end": v(6410, -22) * mm, "construction": true});
            skLineSegment(sketch, "E64.direction2", {"start": v(6385, -22) * mm, "end": v(6385, -12) * mm, "construction": true});
            skLineSegment(sketch, "E65.bottom", {"start": v(6607.5, -22) * mm, "end": v(6830, -22) * mm});
            skLineSegment(sketch, "E65.top", {"start": v(6607.5, -27) * mm, "end": v(6830, -27) * mm});
            skLineSegment(sketch, "E65.left", {"start": v(6607.5, -22) * mm, "end": v(6607.5, -27) * mm});
            skLineSegment(sketch, "E65.right", {"start": v(6830, -22) * mm, "end": v(6830, -27) * mm});
            skLineSegment(sketch, "E66.0.1.0", {"start": v(6607.5, -17) * mm, "end": v(6830, -17) * mm});
            skLineSegment(sketch, "E66.0.1.1", {"start": v(6607.5, -12) * mm, "end": v(6830, -12) * mm});
            skLineSegment(sketch, "E66.0.1.2", {"start": v(6607.5, -12) * mm, "end": v(6607.5, -17) * mm});
            skLineSegment(sketch, "E66.0.1.3", {"start": v(6830, -12) * mm, "end": v(6830, -17) * mm});
            skLineSegment(sketch, "E66.0.2.0", {"start": v(6607.5, -7) * mm, "end": v(6830, -7) * mm});
            skLineSegment(sketch, "E66.0.2.1", {"start": v(6607.5, -2) * mm, "end": v(6830, -2) * mm});
            skLineSegment(sketch, "E66.0.2.2", {"start": v(6607.5, -2) * mm, "end": v(6607.5, -7) * mm});
            skLineSegment(sketch, "E66.0.2.3", {"start": v(6830, -2) * mm, "end": v(6830, -7) * mm});
            skLineSegment(sketch, "E66.direction1", {"start": v(6607.5, -27) * mm, "end": v(6632.5, -27) * mm, "construction": true});
            skLineSegment(sketch, "E66.direction2", {"start": v(6607.5, -27) * mm, "end": v(6607.5, -17) * mm, "construction": true});
            skLineSegment(sketch, "E67", {"start": v(6840, 0) * mm, "end": v(6840, -28.9) * mm});
            skLineSegment(sketch, "E68.MirrorCS", {"start": v(7072.5, -2) * mm, "end": v(6850, -2) * mm});
            skLineSegment(sketch, "E69.MirrorCS", {"start": v(7072.5, -27) * mm, "end": v(6850, -27) * mm});
            skLineSegment(sketch, "E70.MirrorCS", {"start": v(7072.5, -17) * mm, "end": v(6850, -17) * mm});
            skLineSegment(sketch, "E71.MirrorCS", {"start": v(7072.5, -12) * mm, "end": v(6850, -12) * mm});
            skLineSegment(sketch, "E72.MirrorCS", {"start": v(7072.5, -7) * mm, "end": v(6850, -7) * mm});
            skLineSegment(sketch, "E73.MirrorCS", {"start": v(7072.5, -22) * mm, "end": v(6850, -22) * mm});
            skLineSegment(sketch, "E74.MirrorCS", {"start": v(6850, -2) * mm, "end": v(6850, -7) * mm});
            skLineSegment(sketch, "E75.MirrorCS", {"start": v(6850, -22) * mm, "end": v(6850, -27) * mm});
            skLineSegment(sketch, "E76.MirrorCS", {"start": v(6850, -12) * mm, "end": v(6850, -17) * mm});
            skLineSegment(sketch, "E77.MirrorCS", {"start": v(7072.5, -22) * mm, "end": v(7072.5, -27) * mm});
            skLineSegment(sketch, "E78.MirrorCS", {"start": v(7072.5, -27) * mm, "end": v(7072.5, -17) * mm, "construction": true});
            skLineSegment(sketch, "E79.MirrorCS", {"start": v(7072.5, -2) * mm, "end": v(7072.5, -7) * mm});
            skLineSegment(sketch, "E80.MirrorCS", {"start": v(7072.5, -27) * mm, "end": v(7047.5, -27) * mm, "construction": true});
            skLineSegment(sketch, "E81.MirrorCS", {"start": v(7072.5, -12) * mm, "end": v(7072.5, -17) * mm});
            skLineSegment(sketch, "E82.MirrorCS", {"start": v(7295, -22) * mm, "end": v(7295, -27) * mm});
            skLineSegment(sketch, "E83.MirrorCS", {"start": v(7295, -12) * mm, "end": v(7295, -17) * mm});
            skLineSegment(sketch, "E84.MirrorCS", {"start": v(7295, -22) * mm, "end": v(7295, -12) * mm, "construction": true});
            skLineSegment(sketch, "E85.MirrorCS", {"start": v(7092.5, -12) * mm, "end": v(7092.5, -17) * mm});
            skLineSegment(sketch, "E86.MirrorCS", {"start": v(7092.5, -22) * mm, "end": v(7092.5, -27) * mm});
            skLineSegment(sketch, "E87.MirrorCS", {"start": v(7295, -2) * mm, "end": v(7295, -7) * mm});
            skLineSegment(sketch, "E88.MirrorCS", {"start": v(7092.5, -2) * mm, "end": v(7092.5, -7) * mm});
            skLineSegment(sketch, "E89.MirrorCS", {"start": v(7295, -22) * mm, "end": v(7092.5, -22) * mm});
            skLineSegment(sketch, "E90.MirrorCS", {"start": v(7295, -22) * mm, "end": v(7270, -22) * mm, "construction": true});
            skLineSegment(sketch, "E91.MirrorCS", {"start": v(7295, -7) * mm, "end": v(7092.5, -7) * mm});
            skLineSegment(sketch, "E92.MirrorCS", {"start": v(7295, -12) * mm, "end": v(7092.5, -12) * mm});
            skLineSegment(sketch, "E93.MirrorCS", {"start": v(7295, -2) * mm, "end": v(7092.5, -2) * mm});
            skLineSegment(sketch, "E94.MirrorCS", {"start": v(7295, -17) * mm, "end": v(7092.5, -17) * mm});
            skLineSegment(sketch, "E95.MirrorCS", {"start": v(7295, -27) * mm, "end": v(7092.5, -27) * mm});
            skSolve(sketch);
        }
        {
            var Q0;
            Q0=makeQuery(id+"F44.imprint","IMPRINT",FACE,{"disambiguationData":[TD([[makeQuery(id+"F44.imprint","IMPRINT",EDGE,{"derivedFrom":sQuery(id+"F44.wireOp",EDGE,"E63.bottom")}),-1.0]])]});
            var Q1;
            Q1=makeQuery(id+"F44.imprint","IMPRINT",FACE,{"disambiguationData":[TD([[makeQuery(id+"F44.imprint","IMPRINT",EDGE,{"derivedFrom":sQuery(id+"F44.wireOp",EDGE,"E64.0.1.0")}),-1.0]])]});
            var Q2;
            Q2=makeQuery(id+"F44.imprint","IMPRINT",FACE,{"disambiguationData":[TD([[makeQuery(id+"F44.imprint","IMPRINT",EDGE,{"derivedFrom":sQuery(id+"F44.wireOp",EDGE,"E64.0.2.0")}),-1.0]])]});
            var Q3;
            Q3=makeQuery(id+"F44.imprint","IMPRINT",FACE,{"disambiguationData":[TD([[makeQuery(id+"F44.imprint","IMPRINT",EDGE,{"derivedFrom":sQuery(id+"F44.wireOp",EDGE,"E65.bottom")}),-1.0]])]});
            var Q4;
            Q4=makeQuery(id+"F44.imprint","IMPRINT",FACE,{"disambiguationData":[TD([[makeQuery(id+"F44.imprint","IMPRINT",EDGE,{"derivedFrom":sQuery(id+"F44.wireOp",EDGE,"E66.0.1.0")}),1.0]])]});
            var Q5;
            Q5=makeQuery(id+"F44.imprint","IMPRINT",FACE,{"disambiguationData":[TD([[makeQuery(id+"F44.imprint","IMPRINT",EDGE,{"derivedFrom":sQuery(id+"F44.wireOp",EDGE,"E66.0.2.0")}),1.0]])]});
            var Q6;
            Q6=makeQuery(id+"F44.imprint","IMPRINT",FACE,{"disambiguationData":[TD([[makeQuery(id+"F44.imprint","IMPRINT",EDGE,{"derivedFrom":sQuery(id+"F44.wireOp",EDGE,"E74.MirrorCS")}),1.0]])]});
            var Q7;
            Q7=makeQuery(id+"F44.imprint","IMPRINT",FACE,{"disambiguationData":[TD([[makeQuery(id+"F44.imprint","IMPRINT",EDGE,{"derivedFrom":sQuery(id+"F44.wireOp",EDGE,"E76.MirrorCS")}),1.0]])]});
            var Q8;
            Q8=makeQuery(id+"F44.imprint","IMPRINT",FACE,{"disambiguationData":[TD([[makeQuery(id+"F44.imprint","IMPRINT",EDGE,{"derivedFrom":sQuery(id+"F44.wireOp",EDGE,"E75.MirrorCS")}),1.0]])]});
            var Q9;
            Q9=makeQuery(id+"F44.imprint","IMPRINT",FACE,{"disambiguationData":[TD([[makeQuery(id+"F44.imprint","IMPRINT",EDGE,{"derivedFrom":sQuery(id+"F44.wireOp",EDGE,"E87.MirrorCS")}),-1.0]])]});
            var Q10;
            Q10=makeQuery(id+"F44.imprint","IMPRINT",FACE,{"disambiguationData":[TD([[makeQuery(id+"F44.imprint","IMPRINT",EDGE,{"derivedFrom":sQuery(id+"F44.wireOp",EDGE,"E83.MirrorCS")}),-1.0]])]});
            var Q11;
            Q11=makeQuery(id+"F44.imprint","IMPRINT",FACE,{"disambiguationData":[TD([[makeQuery(id+"F44.imprint","IMPRINT",EDGE,{"derivedFrom":sQuery(id+"F44.wireOp",EDGE,"E82.MirrorCS")}),-1.0]])]});
            extrude(context, id + "F45", {"entities" : qUnion([Q0, Q1, Q2, Q3, Q4, Q5, Q6, Q7, Q8, Q9, Q10, Q11]), "operationType" : NewBodyOperationType.REMOVE, "endBound" : BoundingType.UP_TO_NEXT, "oppositeDirection" : true, "depth" : 25 * mm});
        }
        {
            var Q0;
            Q0=makeQuery(id+"F0.imprint","IMPRINT",FACE,{"disambiguationData":[TD([[makeQuery(id+"F0.imprint","IMPRINT",EDGE,{"derivedFrom":sQuery(id+"F0.wireOp",EDGE,"E17.bottom")}),1.0]])]});
            extrude(context, id + "F46", {"entities" : qUnion([Q0]), "depth" : 343 * mm});
        }
        {
            var Q0;
            Q0=makeQuery(id+"F0.imprint","IMPRINT",FACE,{"disambiguationData":[TD([[makeQuery(id+"F0.imprint","IMPRINT",EDGE,{"derivedFrom":sQuery(id+"F0.wireOp",EDGE,"E18.bottom")}),1.0]])]});
            extrude(context, id + "F47", {"entities" : qUnion([Q0]), "depth" : 2000 * mm});
        }
        {
            var Q0;
            Q0=makeQuery(id+"F47.opExtrude","SWEPT_FACE",FACE,{"disambiguationData":[OSD([sQuery(id+"F0.wireOp",EDGE,"E18.top")])]});
            var sketch = newSketch(context, id + "F48", { "sketchPlane" : qUnion([Q0])});
            skPoint(sketch, "E96", {"position": v(7.5, 8327.5) * mm});
            skPoint(sketch, "E97.0.1.0", {"position": v(7.5, 9312.5) * mm});
            skPoint(sketch, "E97.1.0.0", {"position": v(206, 8327.5) * mm});
            skPoint(sketch, "E97.1.1.0", {"position": v(206, 9312.5) * mm});
            skPoint(sketch, "E97.2.0.0", {"position": v(404.5, 8327.5) * mm});
            skPoint(sketch, "E97.2.1.0", {"position": v(404.5, 9312.5) * mm});
            skPoint(sketch, "E97.3.0.0", {"position": v(603, 8327.5) * mm});
            skPoint(sketch, "E97.3.1.0", {"position": v(603, 9312.5) * mm});
            skPoint(sketch, "E97.4.0.0", {"position": v(801.5, 8327.5) * mm});
            skPoint(sketch, "E97.4.1.0", {"position": v(801.5, 9312.5) * mm});
            skPoint(sketch, "E97.5.0.0", {"position": v(1000, 8327.5) * mm});
            skPoint(sketch, "E97.5.1.0", {"position": v(1000, 9312.5) * mm});
            skPoint(sketch, "E97.6.0.0", {"position": v(1198.5, 8327.5) * mm});
            skPoint(sketch, "E97.6.1.0", {"position": v(1198.5, 9312.5) * mm});
            skPoint(sketch, "E97.7.0.0", {"position": v(1397, 8327.5) * mm});
            skPoint(sketch, "E97.7.1.0", {"position": v(1397, 9312.5) * mm});
            skPoint(sketch, "E97.8.0.0", {"position": v(1595.5, 8327.5) * mm});
            skPoint(sketch, "E97.8.1.0", {"position": v(1595.5, 9312.5) * mm});
            skPoint(sketch, "E97.9.0.0", {"position": v(1794, 8327.5) * mm});
            skPoint(sketch, "E97.9.1.0", {"position": v(1794, 9312.5) * mm});
            skPoint(sketch, "E97.10.0.0", {"position": v(1992.5, 8327.5) * mm});
            skPoint(sketch, "E97.10.1.0", {"position": v(1992.5, 9312.5) * mm});
            skLineSegment(sketch, "E97.direction1", {"start": v(7.5, 8327.5) * mm, "end": v(206, 8327.5) * mm, "construction": true});
            skLineSegment(sketch, "E97.direction2", {"start": v(7.5, 8327.5) * mm, "end": v(7.5, 9312.5) * mm, "construction": true});
            skPoint(sketch, "E98.0.1.0", {"position": v(1992.5, 8524.5) * mm});
            skPoint(sketch, "E98.0.2.0", {"position": v(1992.5, 8721.5) * mm});
            skPoint(sketch, "E98.0.3.0", {"position": v(1992.5, 8918.5) * mm});
            skPoint(sketch, "E98.0.4.0", {"position": v(1992.5, 9115.5) * mm});
            skPoint(sketch, "E98.1.1.0", {"position": v(7.5, 8524.5) * mm});
            skPoint(sketch, "E98.1.2.0", {"position": v(7.5, 8721.5) * mm});
            skPoint(sketch, "E98.1.3.0", {"position": v(7.5, 8918.5) * mm});
            skPoint(sketch, "E98.1.4.0", {"position": v(7.5, 9115.5) * mm});
            skLineSegment(sketch, "E98.direction1", {"start": v(1992.5, 8327.5) * mm, "end": v(7.5, 8327.5) * mm, "construction": true});
            skLineSegment(sketch, "E98.direction2", {"start": v(1992.5, 8327.5) * mm, "end": v(1992.5, 8524.5) * mm, "construction": true});
            skSolve(sketch);
        }
        {
            var Q0;
            Q0=sQuery(id+"F48.wireOp",VERTEX,"E96");
            var Q1;
            Q1=sQuery(id+"F48.wireOp",VERTEX,"E97.10.0.0");
            var Q2;
            Q2=sQuery(id+"F48.wireOp",VERTEX,"E97.9.0.0");
            var Q3;
            Q3=sQuery(id+"F48.wireOp",VERTEX,"E97.8.0.0");
            var Q4;
            Q4=sQuery(id+"F48.wireOp",VERTEX,"E97.7.0.0");
            var Q5;
            Q5=sQuery(id+"F48.wireOp",VERTEX,"E97.6.0.0");
            var Q6;
            Q6=sQuery(id+"F48.wireOp",VERTEX,"E97.5.0.0");
            var Q7;
            Q7=sQuery(id+"F48.wireOp",VERTEX,"E97.4.0.0");
            var Q8;
            Q8=sQuery(id+"F48.wireOp",VERTEX,"E97.3.0.0");
            var Q9;
            Q9=sQuery(id+"F48.wireOp",VERTEX,"E97.2.0.0");
            var Q10;
            Q10=sQuery(id+"F48.wireOp",VERTEX,"E97.1.0.0");
            var Q11;
            Q11=sQuery(id+"F48.wireOp",VERTEX,"E98.1.1.0");
            var Q12;
            Q12=sQuery(id+"F48.wireOp",VERTEX,"E98.1.2.0");
            var Q13;
            Q13=sQuery(id+"F48.wireOp",VERTEX,"E98.1.3.0");
            var Q14;
            Q14=sQuery(id+"F48.wireOp",VERTEX,"E98.1.4.0");
            var Q15;
            Q15=sQuery(id+"F48.wireOp",VERTEX,"E97.0.1.0");
            var Q16;
            Q16=sQuery(id+"F48.wireOp",VERTEX,"E97.1.1.0");
            var Q17;
            Q17=sQuery(id+"F48.wireOp",VERTEX,"E97.2.1.0");
            var Q18;
            Q18=sQuery(id+"F48.wireOp",VERTEX,"E97.3.1.0");
            var Q19;
            Q19=sQuery(id+"F48.wireOp",VERTEX,"E97.4.1.0");
            var Q20;
            Q20=sQuery(id+"F48.wireOp",VERTEX,"E97.5.1.0");
            var Q21;
            Q21=sQuery(id+"F48.wireOp",VERTEX,"E97.6.1.0");
            var Q22;
            Q22=sQuery(id+"F48.wireOp",VERTEX,"E97.7.1.0");
            var Q23;
            Q23=sQuery(id+"F48.wireOp",VERTEX,"E97.8.1.0");
            var Q24;
            Q24=sQuery(id+"F48.wireOp",VERTEX,"E97.9.1.0");
            var Q25;
            Q25=sQuery(id+"F48.wireOp",VERTEX,"E97.10.1.0");
            var Q26;
            Q26=sQuery(id+"F48.wireOp",VERTEX,"E98.0.4.0");
            var Q27;
            Q27=sQuery(id+"F48.wireOp",VERTEX,"E98.0.3.0");
            var Q28;
            Q28=sQuery(id+"F48.wireOp",VERTEX,"E98.0.2.0");
            var Q29;
            Q29=sQuery(id+"F48.wireOp",VERTEX,"E98.0.1.0");
            var Q30;
            Q30=makeQuery(id+"F47.opExtrude","SWEPT_BODY",BODY,{"disambiguationData":[OSD([sQuery(id+"F0.wireOp",EDGE,"E18.bottom"),sQuery(id+"F0.wireOp",EDGE,"E18.top"),sQuery(id+"F0.wireOp",EDGE,"E18.left"),sQuery(id+"F0.wireOp",EDGE,"E18.right")])]});
            hole(context, id + "F49", {"style" : HoleStyle.SIMPLE, "endStyle" : HoleEndStyle.THROUGH, "holeDiameter" : 6 * mm, "tappedDepth" : 10.5 * mm, "tapClearance" : 3, "locations" : qUnion([Q0, Q1, Q2, Q3, Q4, Q5, Q6, Q7, Q8, Q9, Q10, Q11, Q12, Q13, Q14, Q15, Q16, Q17, Q18, Q19, Q20, Q21, Q22, Q23, Q24, Q25, Q26, Q27, Q28, Q29]), "scope" : qUnion([Q30])});
        }
        {
            var Q0;
            Q0=makeQuery(id+"F0.imprint","IMPRINT",FACE,{"disambiguationData":[TD([[makeQuery(id+"F0.imprint","IMPRINT",EDGE,{"derivedFrom":sQuery(id+"F0.wireOp",EDGE,"E19.bottom")}),1.0]])]});
            extrude(context, id + "F50", {"entities" : qUnion([Q0]), "depth" : 2000 * mm});
        }
        {
            var Q0;
            Q0=makeQuery(id+"F50.opExtrude","SWEPT_FACE",FACE,{"disambiguationData":[OSD([sQuery(id+"F0.wireOp",EDGE,"E19.top")])]});
            var sketch = newSketch(context, id + "F51", { "sketchPlane" : qUnion([Q0])});
            skPoint(sketch, "E99", {"position": v(7.5, 9347.5) * mm});
            skPoint(sketch, "E99.positionSnap0", {"position": v(0, 9347.5) * mm});
            skPoint(sketch, "E100.1.0.0", {"position": v(206, 9347.5) * mm});
            skPoint(sketch, "E100.2.0.0", {"position": v(404.5, 9347.5) * mm});
            skPoint(sketch, "E100.3.0.0", {"position": v(603, 9347.5) * mm});
            skPoint(sketch, "E100.4.0.0", {"position": v(801.5, 9347.5) * mm});
            skPoint(sketch, "E100.5.0.0", {"position": v(1000, 9347.5) * mm});
            skPoint(sketch, "E100.6.0.0", {"position": v(1198.5, 9347.5) * mm});
            skPoint(sketch, "E100.7.0.0", {"position": v(1397, 9347.5) * mm});
            skPoint(sketch, "E100.8.0.0", {"position": v(1595.5, 9347.5) * mm});
            skPoint(sketch, "E100.9.0.0", {"position": v(1794, 9347.5) * mm});
            skPoint(sketch, "E100.10.0.0", {"position": v(1992.5, 9347.5) * mm});
            skLineSegment(sketch, "E100.direction1", {"start": v(7.5, 9347.5) * mm, "end": v(206, 9347.5) * mm, "construction": true});
            skSolve(sketch);
        }
        {
            var Q0;
            Q0=sQuery(id+"F51.wireOp",VERTEX,"E99");
            var Q1;
            Q1=sQuery(id+"F51.wireOp",VERTEX,"E100.1.0.0");
            var Q2;
            Q2=sQuery(id+"F51.wireOp",VERTEX,"E100.2.0.0");
            var Q3;
            Q3=sQuery(id+"F51.wireOp",VERTEX,"E100.3.0.0");
            var Q4;
            Q4=sQuery(id+"F51.wireOp",VERTEX,"E100.4.0.0");
            var Q5;
            Q5=sQuery(id+"F51.wireOp",VERTEX,"E100.8.0.0");
            var Q6;
            Q6=sQuery(id+"F51.wireOp",VERTEX,"E100.9.0.0");
            var Q7;
            Q7=sQuery(id+"F51.wireOp",VERTEX,"E100.6.0.0");
            var Q8;
            Q8=sQuery(id+"F51.wireOp",VERTEX,"E100.7.0.0");
            var Q9;
            Q9=sQuery(id+"F51.wireOp",VERTEX,"E100.10.0.0");
            var Q10;
            Q10=sQuery(id+"F51.wireOp",VERTEX,"E100.5.0.0");
            var Q11;
            Q11=makeQuery(id+"F50.opExtrude","SWEPT_BODY",BODY,{"disambiguationData":[OSD([sQuery(id+"F0.wireOp",EDGE,"E19.bottom"),sQuery(id+"F0.wireOp",EDGE,"E19.top"),sQuery(id+"F0.wireOp",EDGE,"E19.left"),sQuery(id+"F0.wireOp",EDGE,"E19.right")])]});
            hole(context, id + "F52", {"style" : HoleStyle.SIMPLE, "endStyle" : HoleEndStyle.THROUGH, "holeDiameter" : 2 * mm, "tappedDepth" : 10.5 * mm, "tapClearance" : 3, "locations" : qUnion([Q0, Q1, Q2, Q3, Q4, Q5, Q6, Q7, Q8, Q9, Q10]), "scope" : qUnion([Q11])});
        }
        {
            var Q0;
            Q0=makeQuery(id+"F0.imprint","IMPRINT",FACE,{"disambiguationData":[TD([[makeQuery(id+"F0.imprint","IMPRINT",EDGE,{"derivedFrom":sQuery(id+"F0.wireOp",EDGE,"E20.bottom")}),1.0]])]});
            extrude(context, id + "F53", {"entities" : qUnion([Q0]), "depth" : 970 * mm});
        }
        {
            var Q0;
            Q0=makeQuery(id+"F53.opExtrude","SWEPT_FACE",FACE,{"disambiguationData":[OSD([sQuery(id+"F0.wireOp",EDGE,"E20.top")])]});
            var sketch = newSketch(context, id + "F54", { "sketchPlane" : qUnion([Q0])});
            skPoint(sketch, "E101", {"position": v(189.5, 9382.5) * mm});
            skPoint(sketch, "E101.positionSnap0", {"position": v(0, 9382.5) * mm});
            skPoint(sketch, "E102.1.0.0", {"position": v(386.5, 9382.5) * mm});
            skPoint(sketch, "E102.2.0.0", {"position": v(583.5, 9382.5) * mm});
            skLineSegment(sketch, "E102.direction1", {"start": v(189.5, 9382.5) * mm, "end": v(386.5, 9382.5) * mm, "construction": true});
            skPoint(sketch, "E103.0.3.0", {"position": v(780.5, 9382.5) * mm});
            skSolve(sketch);
        }
        {
            var Q0;
            Q0=sQuery(id+"F54.wireOp",VERTEX,"E103.0.3.0");
            var Q1;
            Q1=sQuery(id+"F54.wireOp",VERTEX,"E102.1.0.0");
            var Q2;
            Q2=sQuery(id+"F54.wireOp",VERTEX,"E102.2.0.0");
            var Q3;
            Q3=sQuery(id+"F54.wireOp",VERTEX,"E101");
            var Q4;
            Q4=makeQuery(id+"F53.opExtrude","SWEPT_BODY",BODY,{"disambiguationData":[OSD([sQuery(id+"F0.wireOp",EDGE,"E20.bottom"),sQuery(id+"F0.wireOp",EDGE,"E20.top"),sQuery(id+"F0.wireOp",EDGE,"E20.left"),sQuery(id+"F0.wireOp",EDGE,"E20.right")])]});
            hole(context, id + "F55", {"style" : HoleStyle.SIMPLE, "endStyle" : HoleEndStyle.THROUGH, "holeDiameter" : 2 * mm, "tappedDepth" : 10.5 * mm, "tapClearance" : 3, "locations" : qUnion([Q0, Q1, Q2, Q3]), "scope" : qUnion([Q4])});
        }
        {
            var Q0;
            Q0=makeQuery(id+"F0.imprint","IMPRINT",FACE,{"disambiguationData":[TD([[makeQuery(id+"F0.imprint","IMPRINT",EDGE,{"derivedFrom":sQuery(id+"F0.wireOp",EDGE,"E21")}),-1.0]])]});
            extrude(context, id + "F56", {"entities" : qUnion([Q0]), "depth" : 2000 * mm});
        }
        {
            var Q0;
            Q0=makeQuery(id+"F0.imprint","IMPRINT",FACE,{"disambiguationData":[TD([[makeQuery(id+"F0.imprint","IMPRINT",EDGE,{"derivedFrom":sQuery(id+"F0.wireOp",EDGE,"E27")}),-1.0]])]});
            extrude(context, id + "F57", {"entities" : qUnion([Q0]), "depth" : 1004 * mm});
        }
        {
            var Q0;
            Q0=makeQuery(id+"F56.opExtrude","SWEPT_FACE",FACE,{"disambiguationData":[OSD([sQuery(id+"F0.wireOp",EDGE,"E23")])]});
            var sketch = newSketch(context, id + "F58", { "sketchPlane" : qUnion([Q0])});
            skLineSegment(sketch, "E104.bottom", {"start": v(-2000, 20) * mm, "end": v(-1982, 20) * mm});
            skLineSegment(sketch, "E104.top", {"start": v(-2000, 2) * mm, "end": v(-1982, 2) * mm});
            skLineSegment(sketch, "E104.left", {"start": v(-2000, 20) * mm, "end": v(-2000, 2) * mm});
            skLineSegment(sketch, "E104.right", {"start": v(-1982, 20) * mm, "end": v(-1982, 2) * mm});
            skLineSegment(sketch, "E105.bottom", {"start": v(0, 2) * mm, "end": v(-18, 2) * mm});
            skLineSegment(sketch, "E105.top", {"start": v(0, 20) * mm, "end": v(-18, 20) * mm});
            skLineSegment(sketch, "E105.left", {"start": v(0, 2) * mm, "end": v(0, 20) * mm});
            skLineSegment(sketch, "E105.right", {"start": v(-18, 2) * mm, "end": v(-18, 20) * mm});
            skSolve(sketch);
        }
        {
            var Q0;
            Q0=makeQuery(id+"F58.imprint","IMPRINT",FACE,{"disambiguationData":[TD([[makeQuery(id+"F58.imprint","IMPRINT",EDGE,{"derivedFrom":sQuery(id+"F58.wireOp",EDGE,"E105.bottom")}),1.0]])]});
            var Q1;
            Q1=makeQuery(id+"F58.imprint","IMPRINT",FACE,{"disambiguationData":[TD([[makeQuery(id+"F58.imprint","IMPRINT",EDGE,{"derivedFrom":sQuery(id+"F58.wireOp",EDGE,"E104.bottom")}),-1.0]])]});
            extrude(context, id + "F59", {"entities" : qUnion([Q0, Q1]), "operationType" : NewBodyOperationType.REMOVE, "endBound" : BoundingType.UP_TO_NEXT, "oppositeDirection" : true, "depth" : 25 * mm});
        }
        {
            var Q0;
            Q0=makeQuery(id+"F57.opExtrude","SWEPT_FACE",FACE,{"disambiguationData":[OSD([sQuery(id+"F0.wireOp",EDGE,"E29")])]});
            var sketch = newSketch(context, id + "F60", { "sketchPlane" : qUnion([Q0])});
            skLineSegment(sketch, "E106.bottom", {"start": v(-1004, 2) * mm, "end": v(-1002, 2) * mm});
            skLineSegment(sketch, "E106.top", {"start": v(-1004, 20) * mm, "end": v(-1002, 20) * mm});
            skLineSegment(sketch, "E106.left", {"start": v(-1004, 2) * mm, "end": v(-1004, 20) * mm});
            skLineSegment(sketch, "E106.right", {"start": v(-1002, 2) * mm, "end": v(-1002, 20) * mm});
            skLineSegment(sketch, "E107.bottom", {"start": v(0, 2) * mm, "end": v(-2, 2) * mm});
            skLineSegment(sketch, "E107.top", {"start": v(0, 20) * mm, "end": v(-2, 20) * mm});
            skLineSegment(sketch, "E107.left", {"start": v(0, 2) * mm, "end": v(0, 20) * mm});
            skLineSegment(sketch, "E107.right", {"start": v(-2, 2) * mm, "end": v(-2, 20) * mm});
            skSolve(sketch);
        }
        {
            var Q0;
            Q0=makeQuery(id+"F60.imprint","IMPRINT",FACE,{"disambiguationData":[TD([[makeQuery(id+"F60.imprint","IMPRINT",EDGE,{"derivedFrom":sQuery(id+"F60.wireOp",EDGE,"E106.bottom")}),1.0]])]});
            var Q1;
            Q1=makeQuery(id+"F60.imprint","IMPRINT",FACE,{"disambiguationData":[TD([[makeQuery(id+"F60.imprint","IMPRINT",EDGE,{"derivedFrom":sQuery(id+"F60.wireOp",EDGE,"E107.bottom")}),1.0]])]});
            extrude(context, id + "F61", {"entities" : qUnion([Q0, Q1]), "operationType" : NewBodyOperationType.REMOVE, "endBound" : BoundingType.UP_TO_NEXT, "oppositeDirection" : true, "depth" : 25 * mm});
        }
    });
